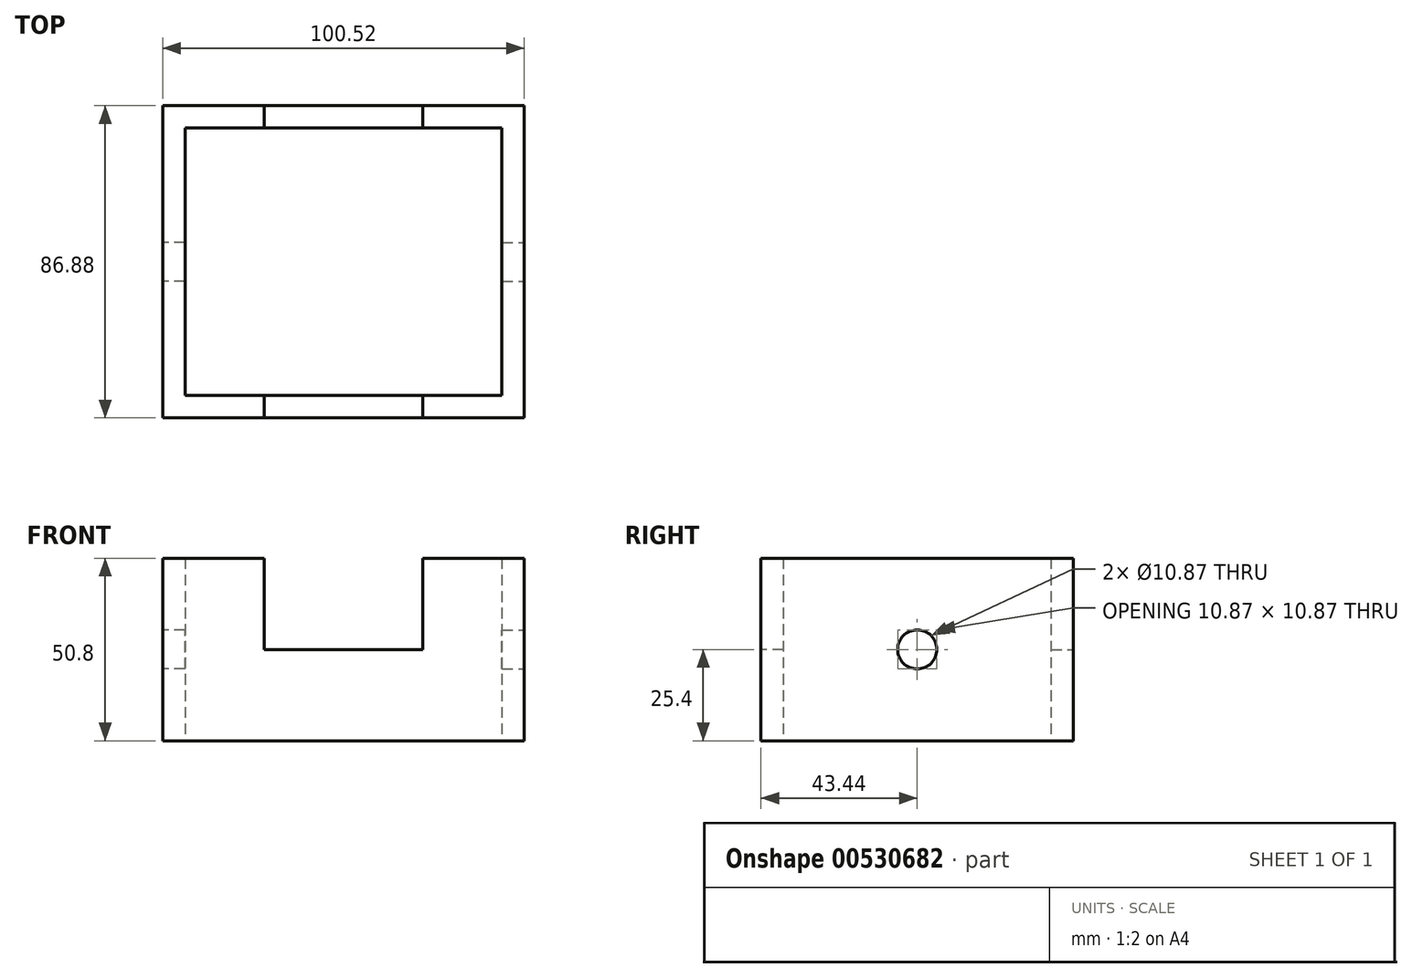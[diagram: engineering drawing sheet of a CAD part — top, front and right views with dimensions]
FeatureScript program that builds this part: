
annotation { "Feature Type Name" : "Feature", "Feature Type Description" : "" }
export const myFeature = defineFeature(function(context is Context, id is Id, definition is map)
    precondition{}
    {
        {
            var Q0;
            Q0=qCreatedBy(makeId("Top.planeOp"),FACE);
            var sketch = newSketch(context, id + "F0", { "sketchPlane" : qUnion([Q0])});
            skLineSegment(sketch, "E0", {"start": v(0, -43.44) * mm, "end": v(-50.26, -43.44) * mm});
            skLineSegment(sketch, "E1", {"start": v(-50.26, -43.44) * mm, "end": v(-50.26, 0) * mm});
            skLineSegment(sketch, "E2", {"start": v(-50.26, 0) * mm, "end": v(-44.02, 0) * mm});
            skLineSegment(sketch, "E3", {"start": v(-44.02, 0) * mm, "end": v(-44.02, -37.2) * mm});
            skLineSegment(sketch, "E4", {"start": v(-44.02, -37.2) * mm, "end": v(0, -37.2) * mm});
            skLineSegment(sketch, "E5", {"start": v(0, -37.2) * mm, "end": v(0, -43.44) * mm});
            skLineSegment(sketch, "E6", {"start": v(-22.01, -37.2) * mm, "end": v(-22.01, -43.44) * mm});
            skSolve(sketch);
        }
        {
            var Q0;
            {var subQ1=sQuery(id+"F0.wireOp",EDGE,"E1");Q0=makeQuery(id+"F0.imprint","IMPRINT",FACE,{"disambiguationData":[TD([[makeQuery(id+"F0.imprint","IMPRINT",EDGE,{"derivedFrom":subQ1}),-1.0]])]});}
            extrude(context, id + "F1", {"entities" : qUnion([Q0]), "depth" : 50.8 * mm, "offsetDistance" : 25.4 * mm});
        }
        {
            var Q0;
            Q0=qSketchRegion(id+"F0",true);
            extrude(context, id + "F2", {"entities" : qUnion([Q0]), "operationType" : NewBodyOperationType.ADD, "depth" : 25.4 * mm, "offsetDistance" : 25.4 * mm});
        }
        {
            var Q0;
            Q0=makeQuery(id+"F1.opExtrude","SWEPT_BODY",BODY,{"disambiguationData":[OSD([sQuery(id+"F0.wireOp",EDGE,"E0"),sQuery(id+"F0.wireOp",EDGE,"E1"),sQuery(id+"F0.wireOp",EDGE,"E2"),sQuery(id+"F0.wireOp",EDGE,"E3"),sQuery(id+"F0.wireOp",EDGE,"E4"),sQuery(id+"F0.wireOp",EDGE,"E6")])]});
            var Q1;
            Q1=qCreatedBy(makeId("Front.planeOp"),FACE);
            mirror(context, id + "F3", {"operationType" : NewBodyOperationType.ADD, "entities" : qUnion([Q0]), "mirrorPlane" : qUnion([Q1])});
        }
        {
            var Q0;
            {var subQ0=makeQuery(id+"F1.opExtrude","SWEPT_FACE",FACE,{"disambiguationData":[OSD([sQuery(id+"F0.wireOp",EDGE,"E1")])]});Q0=makeQuery(id+"F3.boolean.opBoolean","MERGE",FACE,{"derivedFrom":[subQ0,makeQuery(id+"F3.opPattern","COPY",FACE,{"derivedFrom":subQ0,"instanceName":"1"})]});}
            var sketch = newSketch(context, id + "F4", { "sketchPlane" : qUnion([Q0])});
            skLineSegment(sketch, "E7", {"start": v(0, 0) * mm, "end": v(0, 50.8) * mm, "construction": true});
            skCircle(sketch, "E8", {"center": v(0, 25.4) * mm, "radius": 5.44 * mm});
            skSolve(sketch);
        }
        {
            var Q0;
            Q0=makeQuery(id+"F4.imprint","IMPRINT",FACE,{"disambiguationData":[TD([[makeQuery(id+"F4.imprint","IMPRINT",EDGE,{"derivedFrom":sQuery(id+"F4.wireOp",EDGE,"E8")}),1.0]])]});
            extrude(context, id + "F5", {"entities" : qUnion([Q0]), "operationType" : NewBodyOperationType.REMOVE, "endBound" : BoundingType.THROUGH_ALL, "oppositeDirection" : true, "depth" : 25.4 * mm, "offsetDistance" : 25.4 * mm});
        }
        {
            var Q0;
            Q0=makeQuery(id+"F1.opExtrude","SWEPT_BODY",BODY,{"disambiguationData":[OSD([sQuery(id+"F0.wireOp",EDGE,"E0"),sQuery(id+"F0.wireOp",EDGE,"E1"),sQuery(id+"F0.wireOp",EDGE,"E2"),sQuery(id+"F0.wireOp",EDGE,"E3"),sQuery(id+"F0.wireOp",EDGE,"E4"),sQuery(id+"F0.wireOp",EDGE,"E6")])]});
            var Q1;
            Q1=qCreatedBy(makeId("Right.planeOp"),FACE);
            mirror(context, id + "F6", {"operationType" : NewBodyOperationType.ADD, "entities" : qUnion([Q0]), "mirrorPlane" : qUnion([Q1])});
        }
    });
